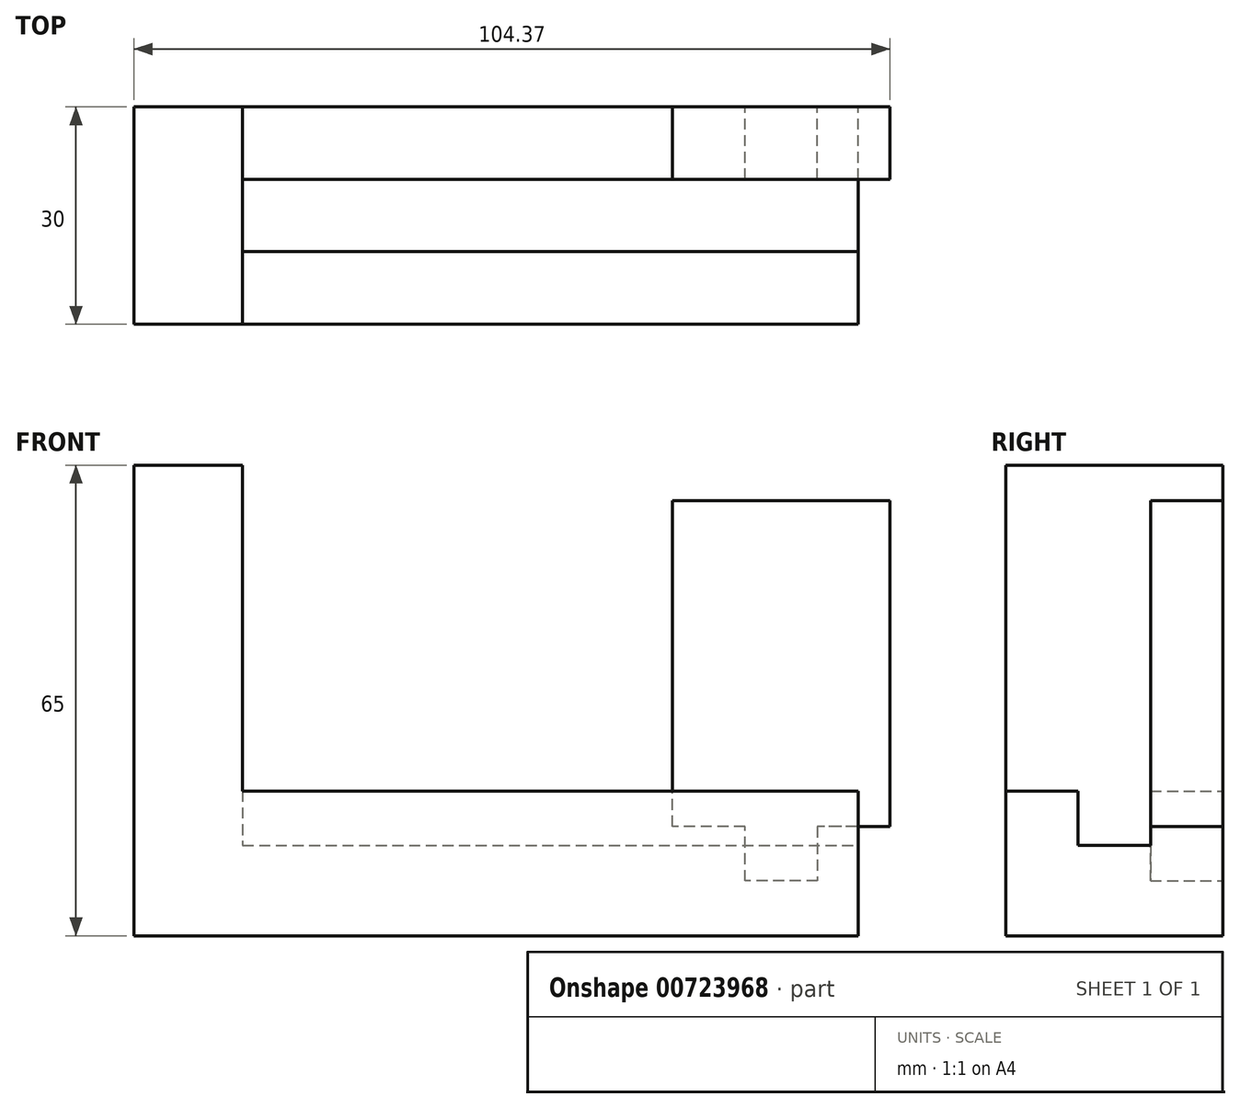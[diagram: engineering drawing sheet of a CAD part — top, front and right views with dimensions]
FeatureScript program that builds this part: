
annotation { "Feature Type Name" : "Feature", "Feature Type Description" : "" }
export const myFeature = defineFeature(function(context is Context, id is Id, definition is map)
    precondition{}
    {
        {
            var Q0;
            Q0=qCreatedBy(makeId("Front.planeOp"),FACE);
            var sketch = newSketch(context, id + "F0", { "sketchPlane" : qUnion([Q0])});
            skLineSegment(sketch, "E0", {"start": v(-48.86, 38.75) * mm, "end": v(-33.86, 38.75) * mm});
            skLineSegment(sketch, "E1", {"start": v(-33.86, 38.75) * mm, "end": v(-33.86, -6.25) * mm});
            skLineSegment(sketch, "E2", {"start": v(-33.86, -6.25) * mm, "end": v(51.14, -6.25) * mm});
            skLineSegment(sketch, "E3", {"start": v(51.14, -6.25) * mm, "end": v(51.14, -26.25) * mm});
            skLineSegment(sketch, "E4", {"start": v(51.14, -26.25) * mm, "end": v(-48.86, -26.25) * mm});
            skLineSegment(sketch, "E5", {"start": v(-48.86, -26.25) * mm, "end": v(-48.86, 38.75) * mm});
            skSolve(sketch);
        }
        {
            var Q0;
            Q0 = qSketchRegion(id + "F0", true);
            extrude(context, id + "F1", {"entities" : qUnion([Q0]), "depth" : 30 * mm, "offsetDistance" : 25 * mm});
        }
        {
            var Q0;
            Q0=qCreatedBy(makeId("Front.planeOp"),FACE);
            var sketch = newSketch(context, id + "F2", { "sketchPlane" : qUnion([Q0])});
            skLineSegment(sketch, "E6", {"start": v(25.5, 33.84) * mm, "end": v(55.5, 33.84) * mm});
            skLineSegment(sketch, "E7", {"start": v(55.5, 33.84) * mm, "end": v(55.5, -11.16) * mm});
            skLineSegment(sketch, "E8", {"start": v(55.5, -11.16) * mm, "end": v(45.5, -11.16) * mm});
            skLineSegment(sketch, "E9", {"start": v(45.5, -11.16) * mm, "end": v(45.5, -18.66) * mm});
            skLineSegment(sketch, "E10", {"start": v(45.5, -18.66) * mm, "end": v(35.5, -18.66) * mm});
            skLineSegment(sketch, "E11", {"start": v(35.5, -18.66) * mm, "end": v(35.5, -11.16) * mm});
            skLineSegment(sketch, "E12", {"start": v(35.5, -11.16) * mm, "end": v(25.5, -11.16) * mm});
            skLineSegment(sketch, "E13", {"start": v(25.5, -11.16) * mm, "end": v(25.5, 33.84) * mm});
            skSolve(sketch);
        }
        {
            var Q0;
            Q0 = qSketchRegion(id + "F2", true);
            extrude(context, id + "F3", {"entities" : qUnion([Q0]), "depth" : 10 * mm, "offsetDistance" : 25 * mm});
        }
        {
            var Q0;
            Q0=makeQuery(id+"F1.opExtrude","SWEPT_FACE",FACE,{"disambiguationData":[OSD([sQuery(id+"F0.wireOp",EDGE,"E3")])]});
            var sketch = newSketch(context, id + "F4", { "sketchPlane" : qUnion([Q0])});
            skLineSegment(sketch, "E14", {"start": v(-20, -6.25) * mm, "end": v(-20, -13.75) * mm});
            skLineSegment(sketch, "E15", {"start": v(-20, -13.75) * mm, "end": v(-10, -13.75) * mm});
            skLineSegment(sketch, "E16", {"start": v(-10, -13.75) * mm, "end": v(-10, -6.25) * mm});
            skLineSegment(sketch, "E17", {"start": v(-20, -6.25) * mm, "end": v(-10, -6.25) * mm});
            skSolve(sketch);
        }
        {
            var Q0;
            Q0=makeQuery(id+"F4.imprint","IMPRINT",FACE,{"disambiguationData":[TD([[makeQuery(id+"F4.imprint","IMPRINT",EDGE,{"derivedFrom":sQuery(id+"F4.wireOp",EDGE,"E14")}),1.0]])]});
            extrude(context, id + "F5", {"entities" : qUnion([Q0]), "operationType" : NewBodyOperationType.REMOVE, "oppositeDirection" : true, "depth" : 85 * mm, "offsetDistance" : 25 * mm});
        }
    });
